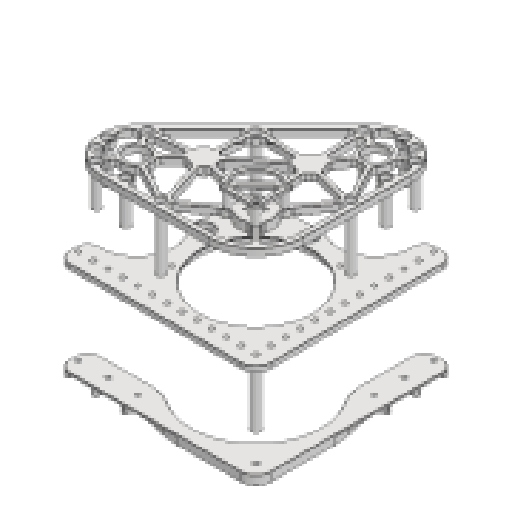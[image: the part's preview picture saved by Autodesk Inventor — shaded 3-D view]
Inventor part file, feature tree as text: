
AUTODESK INVENTOR PART (.ipt)
format: ipt  version: 2023.5 (Build 275446000, 446)  size: 1,824,256 bytes
history: native  units: in
note: dims shown in document units (in); Inventor stores cm internally (conversion verified against a paired STEP export)
features: other x16, chamfer x3, plane x1, move_body x1
ambient origin geometry x8: Origin, YZ Plane, XZ Plane, XY Plane, X Axis, Y Axis, Z Axis, Center Point
bodies: Solid1 (feature_tree), Solid2 (feature_tree), Solid3 (feature_tree), Solid4 (feature_tree), Solid5 (feature_tree), Solid6 (feature_tree), Solid7 (feature_tree), Solid8 (feature_tree), Solid9 (feature_tree), Solid10 (feature_tree), Solid11 (feature_tree), Solid12 (feature_tree), Solid13 (feature_tree), Solid14 (feature_tree), Solid15 (feature_tree), Solid16 (feature_tree), Solid17 (feature_tree), Solid18 (feature_tree), Solid19 (feature_tree)
feature tree (21):
  plane  "Work Plane1"
  move_body  "Move Body1"
  other  "Boss-Extrude4[1]"
  other  "Boss-Extrude4[2]"
  other  "Boss-Extrude4[3]"
  other  "Boss-Extrude6[1]"
  other  "Boss-Extrude6[2]"
  other  "Boss-Extrude6[3]"
  other  "Boss-Extrude6[4]"
  other  "Boss-Extrude6[5]"
  other  "Boss-Extrude6[6]"
  other  "Boss-Extrude6[7]"
  other  "Boss-Extrude6[8]"
  other  "Boss-Extrude9[1]"
  other  "Boss-Extrude17[1]"
  other  "Boss-Extrude17[2]"
  other  "Boss-Extrude17[3]"
  chamfer  "Chamfer4"  [1 undecoded]
  other  "Move Face1"
  chamfer  "Chamfer1"  [1 undecoded]
  chamfer  "Chamfer2"  [1 undecoded]
note: 3 required parameter values undecoded (feature->parameter linkage not recoverable at this tier; creation-order binding heuristic only, values carry confidence <= 0.55)
